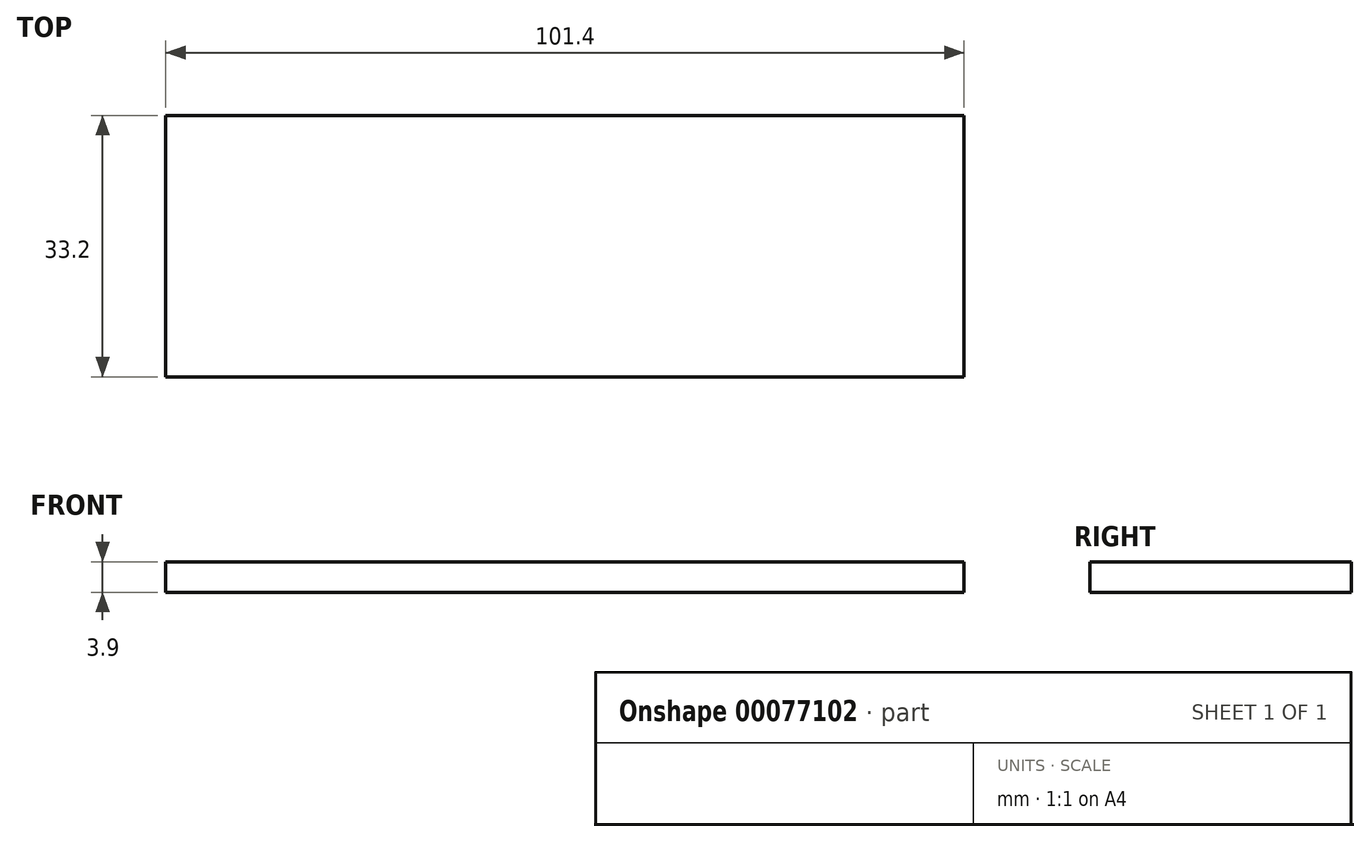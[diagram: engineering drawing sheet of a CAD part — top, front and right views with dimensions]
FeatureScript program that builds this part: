
annotation { "Feature Type Name" : "Feature", "Feature Type Description" : "" }
export const myFeature = defineFeature(function(context is Context, id is Id, definition is map)
    precondition{}
    {
        {
            var Q0;
            Q0=qCreatedBy(makeId("Top.planeOp"),FACE);
            var sketch = newSketch(context, id + "F0", { "sketchPlane" : qUnion([Q0])});
            skLineSegment(sketch, "E0.top", {"start": v(0, 16.6) * mm, "end": v(-50.7, 16.6) * mm});
            skLineSegment(sketch, "E0.right", {"start": v(-50.7, 0) * mm, "end": v(-50.7, 16.6) * mm});
            skPoint(sketch, "E1.right.end.orphan", {"position": v(13.49, 16.6) * mm});
            skPoint(sketch, "E2.top.end.orphan", {"position": v(13.49, -13.8) * mm});
            skPoint(sketch, "E1.bottom.end.orphan", {"position": v(13.49, 0) * mm});
            skPoint(sketch, "E2.left.end.orphan", {"position": v(0, -13.8) * mm});
            skPoint(sketch, "E3.right.end.orphan", {"position": v(-50.7, -13.8) * mm});
            skLineSegment(sketch, "E4.MirrorCS", {"start": v(50.7, 0) * mm, "end": v(50.7, 16.6) * mm});
            skLineSegment(sketch, "E5.MirrorCS", {"start": v(0, 16.6) * mm, "end": v(50.7, 16.6) * mm});
            skLineSegment(sketch, "E6.MirrorCS", {"start": v(-50.7, 0) * mm, "end": v(-50.7, -16.6) * mm});
            skLineSegment(sketch, "E7.MirrorCS", {"start": v(0, -16.6) * mm, "end": v(-50.7, -16.6) * mm});
            skLineSegment(sketch, "E8.MirrorCS", {"start": v(0, -16.6) * mm, "end": v(50.7, -16.6) * mm});
            skLineSegment(sketch, "E9.MirrorCS", {"start": v(50.7, 0) * mm, "end": v(50.7, -16.6) * mm});
            skSolve(sketch);
        }
        {
            var Q0;
            Q0=makeQuery(id+"F0.imprint","IMPRINT",FACE,{"disambiguationData":[TD([[makeQuery(id+"F0.imprint","IMPRINT",EDGE,{"derivedFrom":sQuery(id+"F0.wireOp",EDGE,"E0.top")}),1.0]])]});
            extrude(context, id + "F1", {"entities" : qUnion([Q0]), "depth" : 3.9 * mm, "offsetDistance" : 25 * mm, "symmetric" : true});
        }
    });
